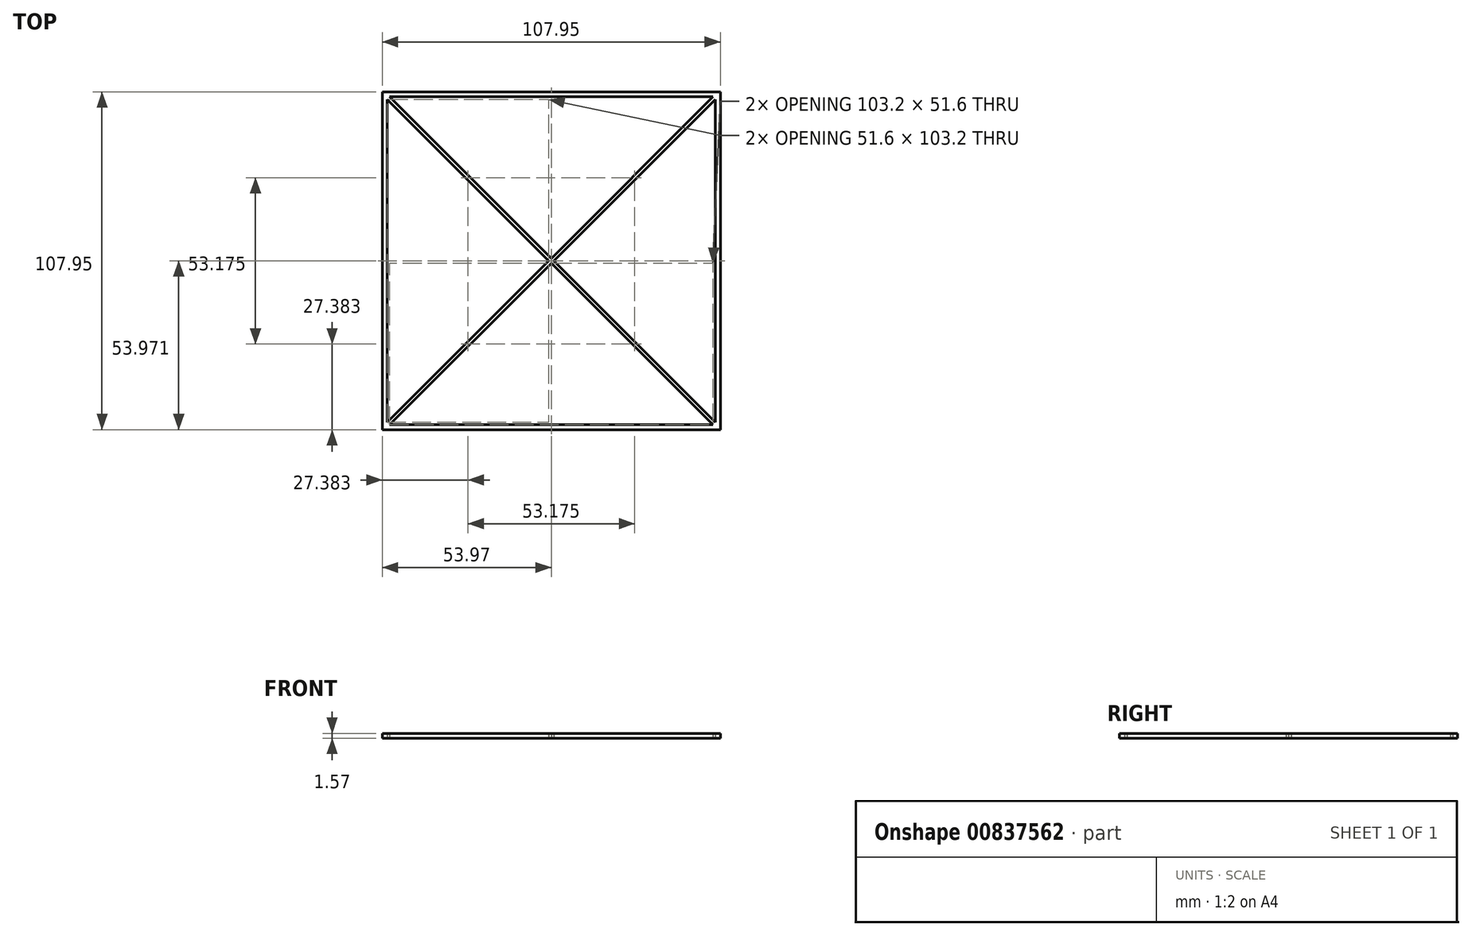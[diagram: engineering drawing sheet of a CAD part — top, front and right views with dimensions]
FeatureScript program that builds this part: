
annotation { "Feature Type Name" : "Feature", "Feature Type Description" : "" }
export const myFeature = defineFeature(function(context is Context, id is Id, definition is map)
    precondition{}
    {
        {
            var Q0;
            Q0=qCreatedBy(makeId("Top.planeOp"),FACE);
            var sketch = newSketch(context, id + "F0", { "sketchPlane" : qUnion([Q0])});
            skLineSegment(sketch, "E0.bottom", {"start": v(-55.32, 47.28) * mm, "end": v(52.63, 47.28) * mm});
            skLineSegment(sketch, "E0.top", {"start": v(-55.32, -60.67) * mm, "end": v(52.63, -60.67) * mm});
            skLineSegment(sketch, "E0.left", {"start": v(-55.32, 47.28) * mm, "end": v(-55.32, -60.67) * mm});
            skLineSegment(sketch, "E0.right", {"start": v(52.63, 47.28) * mm, "end": v(52.63, -60.67) * mm});
            skLineSegment(sketch, "E1.bottom", {"start": v(-52.95, 45.69) * mm, "end": v(50.25, 45.69) * mm});
            skLineSegment(sketch, "E1.top", {"start": v(-52.95, -59.09) * mm, "end": v(50.25, -59.09) * mm});
            skLineSegment(sketch, "E1.left", {"start": v(-53.74, 44.9) * mm, "end": v(-53.74, -58.3) * mm});
            skLineSegment(sketch, "E1.right", {"start": v(51.04, 44.9) * mm, "end": v(51.04, -58.3) * mm});
            skLineSegment(sketch, "E2", {"start": v(-53.74, 44.9) * mm, "end": v(-2.14, -6.7) * mm});
            skLineSegment(sketch, "E3", {"start": v(-52.95, 45.69) * mm, "end": v(-1.35, -5.91) * mm});
            skLineSegment(sketch, "E4", {"start": v(50.25, 45.69) * mm, "end": v(-1.35, -5.91) * mm});
            skLineSegment(sketch, "E5", {"start": v(-52.95, -59.09) * mm, "end": v(-1.35, -7.49) * mm});
            skPoint(sketch, "E6.orphan", {"position": v(-53.74, -59.09) * mm});
            skPoint(sketch, "E7.orphan", {"position": v(51.04, -59.09) * mm});
            skPoint(sketch, "E8.orphan", {"position": v(51.04, 45.69) * mm});
            skPoint(sketch, "E9.orphan", {"position": v(-53.74, 45.69) * mm});
            skLineSegment(sketch, "E10.trimOffspring", {"start": v(-0.56, -6.7) * mm, "end": v(51.04, -58.3) * mm});
            skLineSegment(sketch, "E11.trimOffspring", {"start": v(-2.14, -6.7) * mm, "end": v(-53.74, -58.3) * mm});
            skLineSegment(sketch, "E12.trimOffspring", {"start": v(-1.35, -7.49) * mm, "end": v(50.25, -59.09) * mm});
            skLineSegment(sketch, "E13.trimOffspring", {"start": v(-0.56, -6.7) * mm, "end": v(51.04, 44.9) * mm});
            skSolve(sketch);
        }
        {
            var Q0;
            Q0 = qSketchRegion(id + "F0", true);
            extrude(context, id + "F1", {"entities" : qUnion([Q0]), "depth" : 1.57 * mm, "offsetDistance" : 25.4 * mm});
        }
    });
